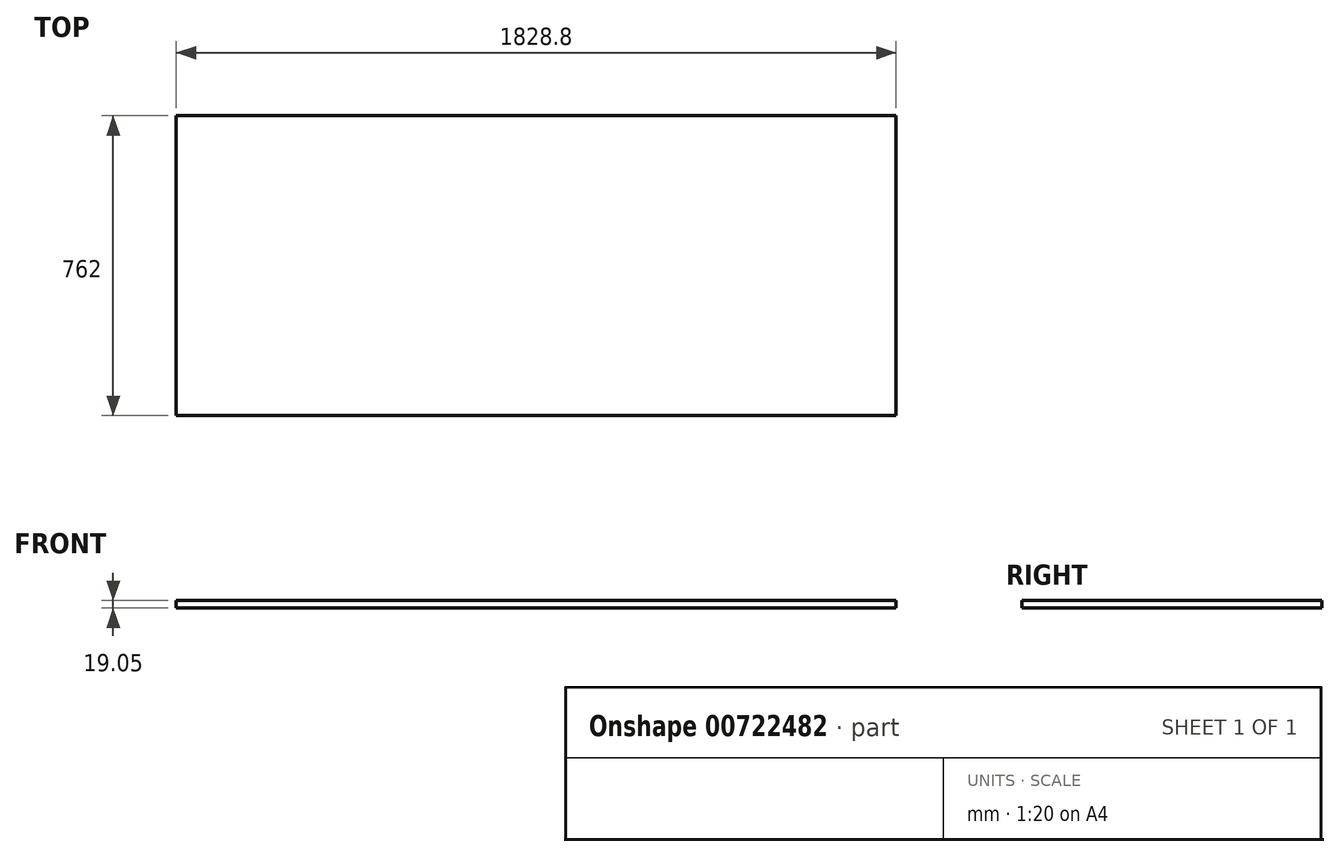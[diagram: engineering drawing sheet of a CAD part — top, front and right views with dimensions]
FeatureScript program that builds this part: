
annotation { "Feature Type Name" : "Feature", "Feature Type Description" : "" }
export const myFeature = defineFeature(function(context is Context, id is Id, definition is map)
    precondition{}
    {
        {
            var Q0;
            Q0=qCreatedBy(makeId("Top.planeOp"),FACE);
            var sketch = newSketch(context, id + "F0", { "sketchPlane" : qUnion([Q0])});
            skLineSegment(sketch, "E0.bottom", {"start": v(0, 0) * mm, "end": v(1828.8, 0) * mm});
            skLineSegment(sketch, "E0.top", {"start": v(0, -762) * mm, "end": v(1828.8, -762) * mm});
            skLineSegment(sketch, "E0.left", {"start": v(0, 0) * mm, "end": v(0, -762) * mm});
            skLineSegment(sketch, "E0.right", {"start": v(1828.8, 0) * mm, "end": v(1828.8, -762) * mm});
            skSolve(sketch);
        }
        {
            var Q0;
            Q0=makeQuery(id+"F0.imprint","IMPRINT",FACE,{"disambiguationData":[TD([[makeQuery(id+"F0.imprint","IMPRINT",EDGE,{"derivedFrom":sQuery(id+"F0.wireOp",EDGE,"E0.bottom")}),-1.0]])]});
            extrude(context, id + "F1", {"entities" : qUnion([Q0]), "oppositeDirection" : true, "depth" : 19.05 * mm, "offsetDistance" : 25.4 * mm});
        }
    });
